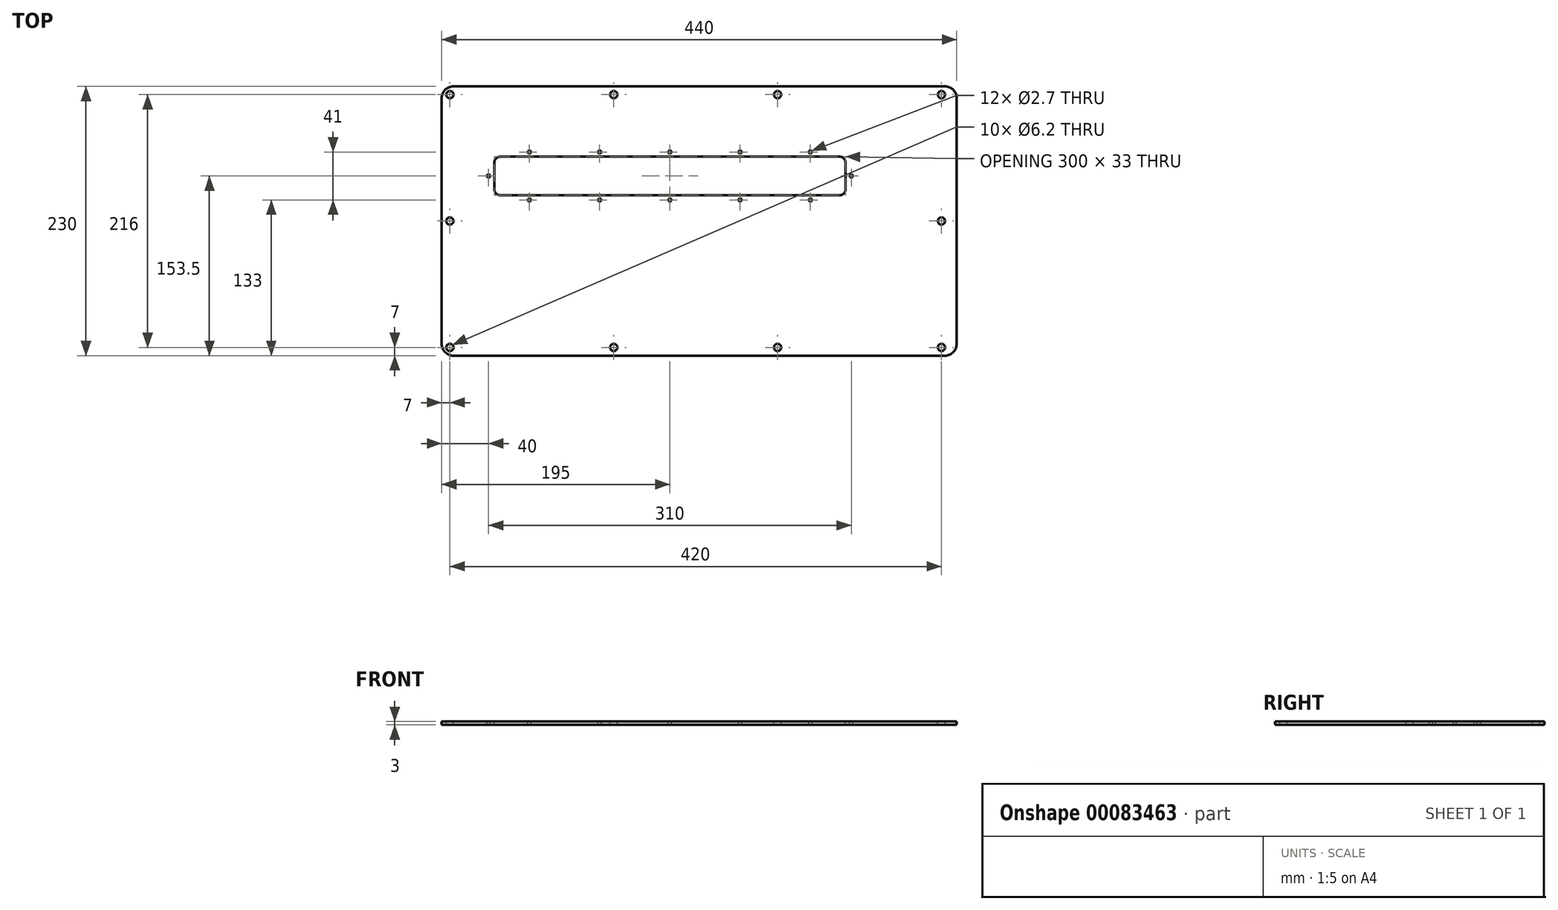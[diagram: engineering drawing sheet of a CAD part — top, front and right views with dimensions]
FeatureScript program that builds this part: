
annotation { "Feature Type Name" : "Feature", "Feature Type Description" : "" }
export const myFeature = defineFeature(function(context is Context, id is Id, definition is map)
    precondition{}
    {
        {
            var Q0;
            Q0=qCreatedBy(makeId("Top.planeOp"),FACE);
            var sketch = newSketch(context, id + "F0", { "sketchPlane" : qUnion([Q0])});
            skLineSegment(sketch, "E0.bottom", {"start": v(0, 0) * mm, "end": v(440, 0) * mm});
            skLineSegment(sketch, "E0.top", {"start": v(0, 230) * mm, "end": v(440, 230) * mm});
            skLineSegment(sketch, "E0.left", {"start": v(0, 0) * mm, "end": v(0, 230) * mm});
            skLineSegment(sketch, "E0.right", {"start": v(440, 0) * mm, "end": v(440, 230) * mm});
            skSolve(sketch);
        }
        {
            var Q0;
            Q0 = qSketchRegion(id + "F0", true);
            extrude(context, id + "F1", {"entities" : qUnion([Q0]), "depth" : 3 * mm});
        }
        {
            var Q0;
            Q0=makeQuery(id+"F1.opExtrude","CAP_FACE",FACE,{"disambiguationData":[OSD([sQuery(id+"F0.wireOp",EDGE,"E0.bottom"),sQuery(id+"F0.wireOp",EDGE,"E0.top"),sQuery(id+"F0.wireOp",EDGE,"E0.left"),sQuery(id+"F0.wireOp",EDGE,"E0.right")])],"isStart":false});
            var sketch = newSketch(context, id + "F2", { "sketchPlane" : qUnion([Q0])});
            skLineSegment(sketch, "E1.bottom", {"start": v(20, 210) * mm, "end": v(420, 210) * mm, "construction": true});
            skLineSegment(sketch, "E1.top", {"start": v(20, 20) * mm, "end": v(420, 20) * mm, "construction": true});
            skLineSegment(sketch, "E1.left", {"start": v(20, 210) * mm, "end": v(20, 20) * mm, "construction": true});
            skLineSegment(sketch, "E1.right", {"start": v(420, 210) * mm, "end": v(420, 20) * mm, "construction": true});
            skLineSegment(sketch, "E2.bottom", {"start": v(30, 182) * mm, "end": v(360, 182) * mm, "construction": true});
            skLineSegment(sketch, "E2.top", {"start": v(30, 125) * mm, "end": v(360, 125) * mm, "construction": true});
            skLineSegment(sketch, "E2.left", {"start": v(30, 182) * mm, "end": v(30, 125) * mm, "construction": true});
            skLineSegment(sketch, "E2.right", {"start": v(360, 182) * mm, "end": v(360, 125) * mm, "construction": true});
            skLineSegment(sketch, "E3.bottom", {"start": v(45, 170) * mm, "end": v(345, 170) * mm});
            skLineSegment(sketch, "E3.top", {"start": v(45, 137) * mm, "end": v(345, 137) * mm});
            skLineSegment(sketch, "E3.left", {"start": v(45, 170) * mm, "end": v(45, 137) * mm});
            skLineSegment(sketch, "E3.right", {"start": v(345, 170) * mm, "end": v(345, 137) * mm});
            skCircle(sketch, "E4", {"center": v(40, 153.5) * mm, "radius": 1.35 * mm});
            skCircle(sketch, "E5", {"center": v(75, 174) * mm, "radius": 1.35 * mm});
            skCircle(sketch, "E6.0.1.0", {"center": v(75, 133) * mm, "radius": 1.35 * mm});
            skCircle(sketch, "E6.1.0.0", {"center": v(135, 174) * mm, "radius": 1.35 * mm});
            skCircle(sketch, "E6.1.1.0", {"center": v(135, 133) * mm, "radius": 1.35 * mm});
            skCircle(sketch, "E6.2.0.0", {"center": v(195, 174) * mm, "radius": 1.35 * mm});
            skCircle(sketch, "E6.2.1.0", {"center": v(195, 133) * mm, "radius": 1.35 * mm});
            skLineSegment(sketch, "E6.direction1", {"start": v(75, 174) * mm, "end": v(135, 174) * mm, "construction": true});
            skLineSegment(sketch, "E6.direction2", {"start": v(75, 174) * mm, "end": v(75, 133) * mm, "construction": true});
            skCircle(sketch, "E7.0.3.0", {"center": v(255, 174) * mm, "radius": 1.35 * mm});
            skCircle(sketch, "E7.0.3.1", {"center": v(255, 133) * mm, "radius": 1.35 * mm});
            skCircle(sketch, "E7.0.4.0", {"center": v(315, 174) * mm, "radius": 1.35 * mm});
            skCircle(sketch, "E7.0.4.1", {"center": v(315, 133) * mm, "radius": 1.35 * mm});
            skCircle(sketch, "E8.1.0.0", {"center": v(350, 153.5) * mm, "radius": 1.35 * mm});
            skLineSegment(sketch, "E8.direction1", {"start": v(40, 153.5) * mm, "end": v(350, 153.5) * mm, "construction": true});
            skCircle(sketch, "E9", {"center": v(7, 7) * mm, "radius": 3.1 * mm});
            skCircle(sketch, "E10.0.1.0", {"center": v(7, 115) * mm, "radius": 3.1 * mm});
            skCircle(sketch, "E10.1.0.0", {"center": v(147, 7) * mm, "radius": 3.1 * mm});
            skCircle(sketch, "E10.2.0.0", {"center": v(287, 7) * mm, "radius": 3.1 * mm});
            skLineSegment(sketch, "E10.direction1", {"start": v(7, 7) * mm, "end": v(147, 7) * mm, "construction": true});
            skLineSegment(sketch, "E10.direction2", {"start": v(7, 7) * mm, "end": v(7, 115) * mm, "construction": true});
            skCircle(sketch, "E11.0.3.0", {"center": v(427, 7) * mm, "radius": 3.1 * mm});
            skCircle(sketch, "E11.0.3.1", {"center": v(427, 115) * mm, "radius": 3.1 * mm});
            skCircle(sketch, "E12.0.0.2", {"center": v(7, 223) * mm, "radius": 3.1 * mm});
            skCircle(sketch, "E12.0.1.2", {"center": v(147, 223) * mm, "radius": 3.1 * mm});
            skCircle(sketch, "E12.0.2.2", {"center": v(287, 223) * mm, "radius": 3.1 * mm});
            skCircle(sketch, "E12.0.3.2", {"center": v(427, 223) * mm, "radius": 3.1 * mm});
            skSolve(sketch);
        }
        {
            var Q0;
            Q0 = qSketchRegion(id + "F2", true);
            extrude(context, id + "F3", {"entities" : qUnion([Q0]), "operationType" : NewBodyOperationType.REMOVE, "endBound" : BoundingType.THROUGH_ALL, "oppositeDirection" : true, "depth" : 25 * mm});
        }
        {
            var Q0;
            Q0=makeQuery(id+"F1.opExtrude","SWEPT_EDGE",EDGE,{"disambiguationData":[OSD([sQuery(id+"F0.wireOp",EDGE,"E0.bottom"),sQuery(id+"F0.wireOp",EDGE,"E0.right")])]});
            var Q1;
            Q1=makeQuery(id+"F1.opExtrude","SWEPT_EDGE",EDGE,{"disambiguationData":[OSD([sQuery(id+"F0.wireOp",EDGE,"E0.bottom"),sQuery(id+"F0.wireOp",EDGE,"E0.left")])]});
            var Q2;
            Q2=makeQuery(id+"F1.opExtrude","SWEPT_EDGE",EDGE,{"disambiguationData":[OSD([sQuery(id+"F0.wireOp",EDGE,"E0.top"),sQuery(id+"F0.wireOp",EDGE,"E0.right")])]});
            var Q3;
            Q3=makeQuery(id+"F1.opExtrude","SWEPT_EDGE",EDGE,{"disambiguationData":[OSD([sQuery(id+"F0.wireOp",EDGE,"E0.top"),sQuery(id+"F0.wireOp",EDGE,"E0.left")])]});
            fillet(context, id + "F4", {"entities" : qUnion([Q0, Q1, Q2, Q3]), "radius" : 10 * mm, "tangentPropagation" : true, "allowEdgeOverflow" : false});
        }
        {
            var Q0;
            Q0=makeQuery(id+"F3.boolean.opBoolean","COPY",EDGE,{"derivedFrom":makeQuery(id+"F3.opExtrude","SWEPT_EDGE",EDGE,{"disambiguationData":[OSD([sQuery(id+"F2.wireOp",EDGE,"E3.top"),sQuery(id+"F2.wireOp",EDGE,"E3.left")])]})});
            var Q1;
            Q1=makeQuery(id+"F3.boolean.opBoolean","COPY",EDGE,{"derivedFrom":makeQuery(id+"F3.opExtrude","SWEPT_EDGE",EDGE,{"disambiguationData":[OSD([sQuery(id+"F2.wireOp",EDGE,"E3.bottom"),sQuery(id+"F2.wireOp",EDGE,"E3.left")])]})});
            var Q2;
            Q2=makeQuery(id+"F3.boolean.opBoolean","COPY",EDGE,{"derivedFrom":makeQuery(id+"F3.opExtrude","SWEPT_EDGE",EDGE,{"disambiguationData":[OSD([sQuery(id+"F2.wireOp",EDGE,"E3.bottom"),sQuery(id+"F2.wireOp",EDGE,"E3.right")])]})});
            var Q3;
            Q3=makeQuery(id+"F3.boolean.opBoolean","COPY",EDGE,{"derivedFrom":makeQuery(id+"F3.opExtrude","SWEPT_EDGE",EDGE,{"disambiguationData":[OSD([sQuery(id+"F2.wireOp",EDGE,"E3.top"),sQuery(id+"F2.wireOp",EDGE,"E3.right")])]})});
            fillet(context, id + "F5", {"entities" : qUnion([Q0, Q1, Q2, Q3]), "radius" : 5 * mm, "tangentPropagation" : true, "allowEdgeOverflow" : false});
        }
    });
